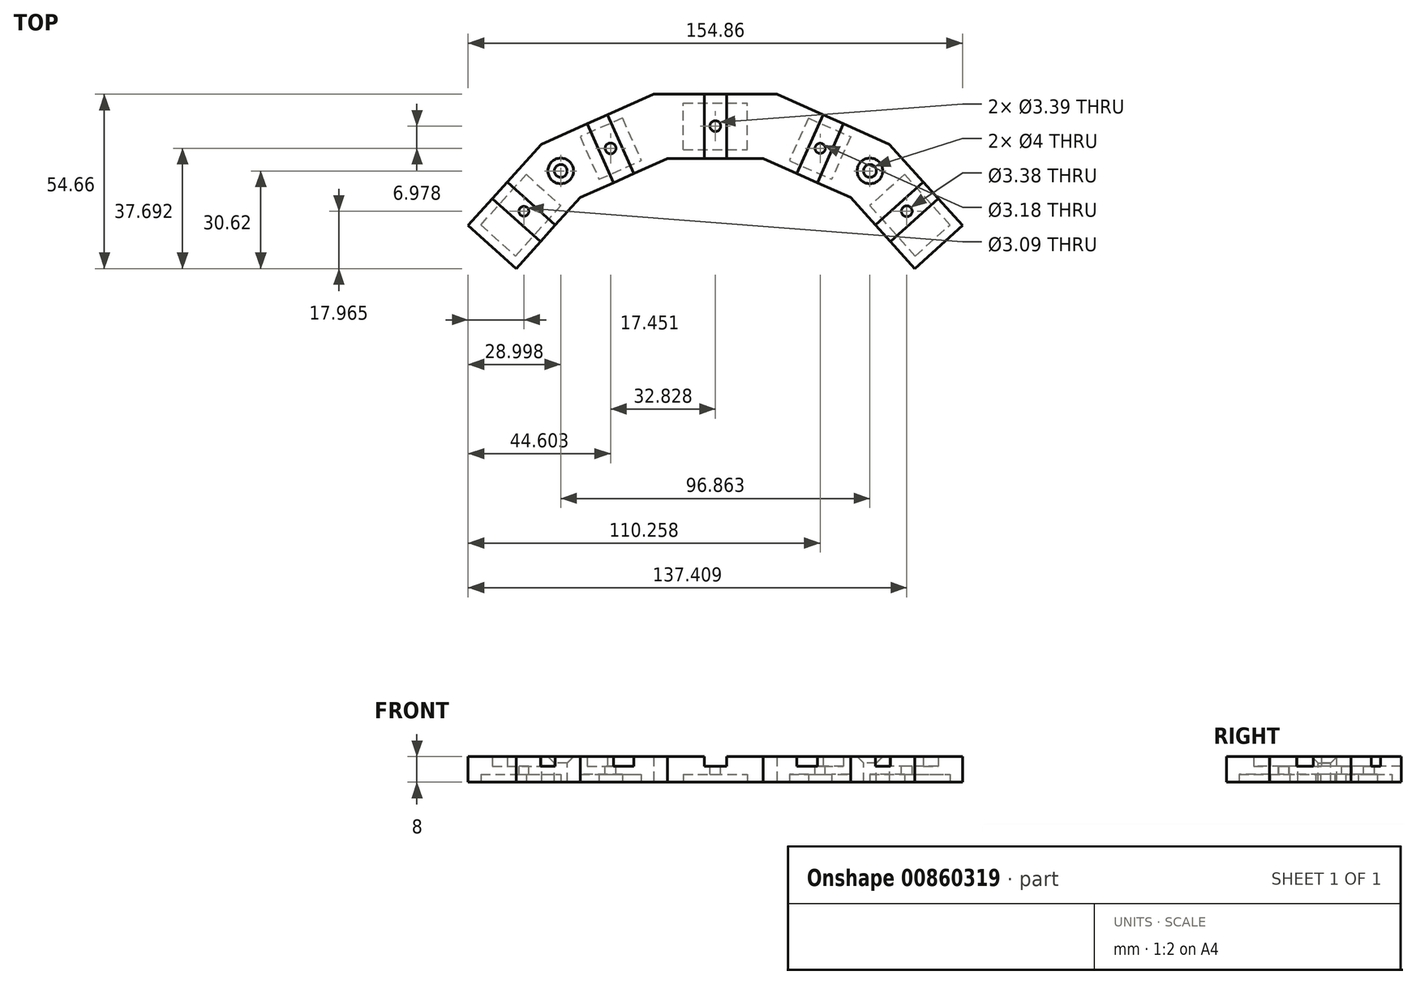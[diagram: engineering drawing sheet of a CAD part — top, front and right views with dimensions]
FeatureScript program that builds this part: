
annotation { "Feature Type Name" : "Feature", "Feature Type Description" : "" }
export const myFeature = defineFeature(function(context is Context, id is Id, definition is map)
    precondition{}
    {
        {
            var Q0;
            Q0=qCreatedBy(makeId("Top.planeOp"),FACE);
            var sketch = newSketch(context, id + "F0", { "sketchPlane" : qUnion([Q0])});
            skLineSegment(sketch, "E0.0", {"start": v(-14.98, 70.5) * mm, "end": v(14.98, 70.5) * mm});
            skLineSegment(sketch, "E0.1", {"start": v(14.98, 70.5) * mm, "end": v(42.36, 58.3) * mm});
            skLineSegment(sketch, "E0.2", {"start": v(42.36, 58.3) * mm, "end": v(62.42, 36.04) * mm});
            skLineSegment(sketch, "E0.13", {"start": v(-62.42, 36.04) * mm, "end": v(-42.36, 58.3) * mm});
            skLineSegment(sketch, "E0.14", {"start": v(-42.36, 58.3) * mm, "end": v(-14.98, 70.5) * mm});
            skPoint(sketch, "E0.0.midPoint", {"position": v(0, 70.5) * mm});
            skLineSegment(sketch, "E1.0", {"start": v(54.5, 75.01) * mm, "end": v(77.43, 49.55) * mm});
            skLineSegment(sketch, "E1.1", {"start": v(-77.43, 49.55) * mm, "end": v(-54.5, 75.01) * mm});
            skLineSegment(sketch, "E1.2", {"start": v(-54.5, 75.01) * mm, "end": v(-19.28, 90.7) * mm});
            skLineSegment(sketch, "E1.3", {"start": v(-19.28, 90.7) * mm, "end": v(19.28, 90.7) * mm});
            skLineSegment(sketch, "E1.4", {"start": v(19.28, 90.7) * mm, "end": v(54.5, 75.01) * mm});
            skLineSegment(sketch, "E2", {"start": v(-77.43, 49.55) * mm, "end": v(-62.42, 36.04) * mm});
            skLineSegment(sketch, "E3", {"start": v(62.42, 36.04) * mm, "end": v(77.43, 49.55) * mm});
            skPoint(sketch, "E0.cCircle.center.orphan", {"position": v(0, 0) * mm});
            skSolve(sketch);
        }
        {
            var Q0;
            Q0 = qSketchRegion(id + "F0", true);
            extrude(context, id + "F1", {"entities" : qUnion([Q0]), "depth" : 5 * mm, "offsetDistance" : 25 * mm});
        }
        {
            var Q0;
            Q0=makeQuery(id+"F1.opExtrude","CAP_FACE",FACE,{"disambiguationData":[OSD([sQuery(id+"F0.wireOp",EDGE,"E0.0"),sQuery(id+"F0.wireOp",EDGE,"E0.1"),sQuery(id+"F0.wireOp",EDGE,"E0.2"),sQuery(id+"F0.wireOp",EDGE,"E0.13"),sQuery(id+"F0.wireOp",EDGE,"E0.14"),sQuery(id+"F0.wireOp",EDGE,"E1.0"),sQuery(id+"F0.wireOp",EDGE,"E1.1"),sQuery(id+"F0.wireOp",EDGE,"E1.2"),sQuery(id+"F0.wireOp",EDGE,"E1.3"),sQuery(id+"F0.wireOp",EDGE,"E1.4"),sQuery(id+"F0.wireOp",EDGE,"E2"),sQuery(id+"F0.wireOp",EDGE,"E3")])],"isStart":false});
            var sketch = newSketch(context, id + "F2", { "sketchPlane" : qUnion([Q0])});
            skLineSegment(sketch, "E4", {"start": v(0, 90.7) * mm, "end": v(0, 70.5) * mm});
            skLineSegment(sketch, "E5.left", {"start": v(3.5, 90.7) * mm, "end": v(3.5, 70.5) * mm});
            skLineSegment(sketch, "E5.right", {"start": v(-3.5, 90.7) * mm, "end": v(-3.5, 70.5) * mm});
            skPoint(sketch, "E5.middle", {"position": v(0, 80.6) * mm});
            skPoint(sketch, "E6.center", {"position": v(0, 0) * mm});
            skLineSegment(sketch, "E7.1.1", {"start": v(33.76, 84.25) * mm, "end": v(25.53, 65.8) * mm});
            skLineSegment(sketch, "E7.1.2", {"start": v(40.16, 81.4) * mm, "end": v(31.93, 62.95) * mm});
            skLineSegment(sketch, "E7.2.1", {"start": v(65.16, 63.17) * mm, "end": v(50.13, 49.68) * mm});
            skLineSegment(sketch, "E7.2.2", {"start": v(69.85, 57.97) * mm, "end": v(54.81, 44.48) * mm});
            skLineSegment(sketch, "E8.MirrorCS", {"start": v(-33.76, 84.25) * mm, "end": v(-25.53, 65.8) * mm});
            skLineSegment(sketch, "E9.MirrorCS", {"start": v(-40.16, 81.4) * mm, "end": v(-31.93, 62.95) * mm});
            skLineSegment(sketch, "E10.MirrorCS", {"start": v(-69.85, 57.97) * mm, "end": v(-54.81, 44.48) * mm});
            skLineSegment(sketch, "E11.MirrorCS", {"start": v(-65.16, 63.17) * mm, "end": v(-50.13, 49.68) * mm});
            skLineSegment(sketch, "E12", {"start": v(-69.85, 57.97) * mm, "end": v(-77.43, 49.55) * mm});
            skLineSegment(sketch, "E13", {"start": v(-77.43, 49.55) * mm, "end": v(-62.42, 36.04) * mm});
            skLineSegment(sketch, "E14", {"start": v(-62.42, 36.04) * mm, "end": v(-54.81, 44.48) * mm});
            skPoint(sketch, "E15.MirrorCS.end.orphan", {"position": v(-65.16, 63.17) * mm});
            skPoint(sketch, "E16.MirrorCS.end.orphan", {"position": v(-50.13, 49.68) * mm});
            skPoint(sketch, "E16.MirrorCS.start.orphan", {"position": v(-54.81, 44.48) * mm});
            skLineSegment(sketch, "E17", {"start": v(-65.16, 63.17) * mm, "end": v(-54.5, 75.01) * mm});
            skLineSegment(sketch, "E18", {"start": v(-54.5, 75.01) * mm, "end": v(-40.16, 81.4) * mm});
            skLineSegment(sketch, "E19", {"start": v(-31.93, 62.95) * mm, "end": v(-42.36, 58.3) * mm});
            skLineSegment(sketch, "E20", {"start": v(-42.36, 58.3) * mm, "end": v(-50.13, 49.68) * mm});
            skLineSegment(sketch, "E21", {"start": v(-33.76, 84.25) * mm, "end": v(-19.28, 90.7) * mm});
            skLineSegment(sketch, "E22", {"start": v(-19.28, 90.7) * mm, "end": v(-3.5, 90.7) * mm});
            skLineSegment(sketch, "E23", {"start": v(-3.5, 70.5) * mm, "end": v(-14.98, 70.5) * mm});
            skLineSegment(sketch, "E24", {"start": v(-14.98, 70.5) * mm, "end": v(-25.53, 65.8) * mm});
            skLineSegment(sketch, "E25", {"start": v(3.5, 90.7) * mm, "end": v(19.28, 90.7) * mm});
            skLineSegment(sketch, "E26", {"start": v(19.28, 90.7) * mm, "end": v(33.76, 84.25) * mm});
            skLineSegment(sketch, "E27", {"start": v(3.5, 70.5) * mm, "end": v(14.98, 70.5) * mm});
            skLineSegment(sketch, "E28", {"start": v(14.98, 70.5) * mm, "end": v(25.53, 65.8) * mm});
            skLineSegment(sketch, "E29", {"start": v(40.16, 81.4) * mm, "end": v(54.5, 75.01) * mm});
            skLineSegment(sketch, "E30", {"start": v(54.5, 75.01) * mm, "end": v(65.16, 63.17) * mm});
            skLineSegment(sketch, "E31", {"start": v(31.93, 62.95) * mm, "end": v(42.36, 58.3) * mm});
            skLineSegment(sketch, "E32", {"start": v(42.36, 58.3) * mm, "end": v(50.13, 49.68) * mm});
            skLineSegment(sketch, "E33", {"start": v(69.85, 57.97) * mm, "end": v(77.43, 49.55) * mm});
            skLineSegment(sketch, "E34", {"start": v(77.43, 49.55) * mm, "end": v(62.42, 36.04) * mm});
            skLineSegment(sketch, "E35", {"start": v(62.42, 36.04) * mm, "end": v(54.81, 44.48) * mm});
            skPoint(sketch, "E36.MirrorCS.end.orphan", {"position": v(-33.76, 84.25) * mm});
            skPoint(sketch, "E36.MirrorCS.start.orphan", {"position": v(-40.16, 81.4) * mm});
            skPoint(sketch, "E37.MirrorCS.end.orphan", {"position": v(-25.53, 65.8) * mm});
            skPoint(sketch, "E37.MirrorCS.start.orphan", {"position": v(-31.93, 62.95) * mm});
            skSolve(sketch);
        }
        {
            var Q0;
            Q0 = qSketchRegion(id + "F2", true);
            var Q1;
            Q1=makeQuery(id+"F2.imprint","IMPRINT",FACE,{"disambiguationData":[TD([[makeQuery(id+"F2.imprint","IMPRINT",EDGE,{"derivedFrom":sQuery(id+"F2.wireOp",EDGE,"E5.right")}),-1.0]])]});
            extrude(context, id + "F3", {"entities" : qUnion([Q0, Q1]), "operationType" : NewBodyOperationType.ADD, "depth" : 3 * mm, "offsetDistance" : 25 * mm});
        }
        {
            var Q0;
            {var subQ0=sQuery(id+"F0.wireOp",EDGE,"E1.2");var subQ1=sQuery(id+"F0.wireOp",EDGE,"E0.14");Q0=makeQuery(id+"F3.boolean.opBoolean","SPLIT",FACE,{"disambiguationData":[TD([makeQuery(id+"F1.opExtrude","SWEPT_FACE",FACE,{"disambiguationData":[OSD([subQ1])]})])],"derivedFrom":makeQuery(id+"F1.opExtrude","CAP_FACE",FACE,{"disambiguationData":[OSD([sQuery(id+"F0.wireOp",EDGE,"E0.0"),sQuery(id+"F0.wireOp",EDGE,"E0.1"),sQuery(id+"F0.wireOp",EDGE,"E0.2"),sQuery(id+"F0.wireOp",EDGE,"E0.13"),subQ1,sQuery(id+"F0.wireOp",EDGE,"E1.0"),sQuery(id+"F0.wireOp",EDGE,"E1.1"),subQ0,sQuery(id+"F0.wireOp",EDGE,"E1.3"),sQuery(id+"F0.wireOp",EDGE,"E1.4"),sQuery(id+"F0.wireOp",EDGE,"E2"),sQuery(id+"F0.wireOp",EDGE,"E3")])],"isStart":false})});}
            var sketch = newSketch(context, id + "F4", { "sketchPlane" : qUnion([Q0])});
            skLineSegment(sketch, "E38", {"start": v(0, 90.78) * mm, "end": v(0, 70.64) * mm});
            skPoint(sketch, "E39", {"position": v(0, 80.7) * mm});
            skPoint(sketch, "E40.1.0", {"position": v(32.83, 73.73) * mm});
            skPoint(sketch, "E40.2.0", {"position": v(59.98, 54) * mm});
            skPoint(sketch, "E40.center", {"position": v(0, 0) * mm});
            skLineSegment(sketch, "E40.anchor1", {"start": v(0, 0) * mm, "end": v(0, 80.7) * mm, "construction": true});
            skLineSegment(sketch, "E40.anchor2", {"start": v(0, 0) * mm, "end": v(59.98, 54) * mm, "construction": true});
            skPoint(sketch, "E41.MirrorP", {"position": v(-32.83, 73.73) * mm});
            skPoint(sketch, "E42.MirrorP", {"position": v(-59.98, 54) * mm});
            skCircle(sketch, "E43", {"center": v(-59.98, 54) * mm, "radius": 1.55 * mm});
            skCircle(sketch, "E44", {"center": v(-32.83, 73.73) * mm, "radius": 1.7 * mm});
            skCircle(sketch, "E45", {"center": v(0, 80.7) * mm, "radius": 1.7 * mm});
            skCircle(sketch, "E46", {"center": v(32.83, 73.73) * mm, "radius": 1.6 * mm});
            skCircle(sketch, "E47", {"center": v(59.98, 54) * mm, "radius": 1.69 * mm});
            skSolve(sketch);
        }
        {
            var Q0;
            Q0=makeQuery(id+"F3.opExtrude","CAP_FACE",FACE,{"disambiguationData":[OSD([sQuery(id+"F2.wireOp",EDGE,"E9.MirrorCS"),sQuery(id+"F2.wireOp",EDGE,"E11.MirrorCS"),sQuery(id+"F2.wireOp",EDGE,"E17"),sQuery(id+"F2.wireOp",EDGE,"E18"),sQuery(id+"F2.wireOp",EDGE,"E19"),sQuery(id+"F2.wireOp",EDGE,"E20")])],"isStart":false});
            var sketch = newSketch(context, id + "F5", { "sketchPlane" : qUnion([Q0])});
            skLineSegment(sketch, "E48", {"start": v(-54.5, 75.01) * mm, "end": v(-42.36, 58.3) * mm});
            skPoint(sketch, "E49", {"position": v(-48.43, 66.66) * mm});
            skLineSegment(sketch, "E50", {"start": v(0, 91.15) * mm, "end": v(0, 71.4) * mm});
            skPoint(sketch, "E51.MirrorP", {"position": v(48.43, 66.66) * mm});
            skSolve(sketch);
        }
        {
            var Q0;
            Q0=sQuery(id+"F5.wireOp",VERTEX,"E49");
            var Q1;
            Q1=sQuery(id+"F5.wireOp",VERTEX,"E51.MirrorP");
            var Q2;
            Q2=makeQuery(id+"F1.opExtrude","SWEPT_BODY",BODY,{"disambiguationData":[OSD([sQuery(id+"F0.wireOp",EDGE,"E0.0"),sQuery(id+"F0.wireOp",EDGE,"E0.1"),sQuery(id+"F0.wireOp",EDGE,"E0.2"),sQuery(id+"F0.wireOp",EDGE,"E0.13"),sQuery(id+"F0.wireOp",EDGE,"E0.14"),sQuery(id+"F0.wireOp",EDGE,"E1.0"),sQuery(id+"F0.wireOp",EDGE,"E1.1"),sQuery(id+"F0.wireOp",EDGE,"E1.2"),sQuery(id+"F0.wireOp",EDGE,"E1.3"),sQuery(id+"F0.wireOp",EDGE,"E1.4"),sQuery(id+"F0.wireOp",EDGE,"E2"),sQuery(id+"F0.wireOp",EDGE,"E3")])]});
            hole(context, id + "F6", {"style" : HoleStyle.C_SINK, "endStyle" : HoleEndStyle.THROUGH, "standardTappedOrClearance" : lookupTablePath({ "standard" : "ISO", "size" : "4", "type" : "Drilled" }), "standardBlindInLast" : lookupTablePath({ "standard" : "ISO", "size" : "4", "type" : "Drilled" }), "holeDiameter" : 4 * mm, "cSinkDiameter" : 8 * mm, "cSinkAngle" : 90 * degree, "majorDiameter" : 5 * mm, "isTappedThrough" : true, "tappedDepth" : 12 * mm, "tapClearance" : 3, "locations" : qUnion([Q0, Q1]), "scope" : qUnion([Q2])});
        }
        {
            var Q0;
            Q0 = qSketchRegion(id + "F4", true);
            extrude(context, id + "F7", {"entities" : qUnion([Q0]), "operationType" : NewBodyOperationType.REMOVE, "oppositeDirection" : true, "depth" : 11.1 * mm, "offsetDistance" : 25 * mm});
        }
        {
            var Q0;
            Q0=makeQuery(id+"F1.opExtrude","CAP_FACE",FACE,{"disambiguationData":[OSD([sQuery(id+"F0.wireOp",EDGE,"E0.0"),sQuery(id+"F0.wireOp",EDGE,"E0.1"),sQuery(id+"F0.wireOp",EDGE,"E0.2"),sQuery(id+"F0.wireOp",EDGE,"E0.13"),sQuery(id+"F0.wireOp",EDGE,"E0.14"),sQuery(id+"F0.wireOp",EDGE,"E1.0"),sQuery(id+"F0.wireOp",EDGE,"E1.1"),sQuery(id+"F0.wireOp",EDGE,"E1.2"),sQuery(id+"F0.wireOp",EDGE,"E1.3"),sQuery(id+"F0.wireOp",EDGE,"E1.4"),sQuery(id+"F0.wireOp",EDGE,"E2"),sQuery(id+"F0.wireOp",EDGE,"E3")])],"isStart":true});
            var sketch = newSketch(context, id + "F8", { "sketchPlane" : qUnion([Q0])});
            skLineSegment(sketch, "E52.1", {"start": v(48.4, -55.78) * mm, "end": v(62.62, -39.99) * mm});
            skLineSegment(sketch, "E52.2", {"start": v(62.62, -39.99) * mm, "end": v(73.47, -49.76) * mm});
            skLineSegment(sketch, "E52.3", {"start": v(59.26, -65.55) * mm, "end": v(73.47, -49.76) * mm});
            skLineSegment(sketch, "E52.4", {"start": v(29.14, -83.24) * mm, "end": v(42.36, -77.35) * mm});
            skLineSegment(sketch, "E52.5", {"start": v(23.2, -69.9) * mm, "end": v(36.42, -64.02) * mm});
            skLineSegment(sketch, "E52.6", {"start": v(-10.05, -87.9) * mm, "end": v(10.05, -87.9) * mm});
            skLineSegment(sketch, "E52.7", {"start": v(0, -73.3) * mm, "end": v(10.05, -73.3) * mm});
            skLineSegment(sketch, "E52.8", {"start": v(-36.42, -64.02) * mm, "end": v(-23.2, -69.9) * mm});
            skLineSegment(sketch, "E52.9", {"start": v(-62.62, -39.99) * mm, "end": v(-48.4, -55.78) * mm});
            skLineSegment(sketch, "E52.10", {"start": v(-73.47, -49.76) * mm, "end": v(-62.62, -39.99) * mm});
            skLineSegment(sketch, "E52.11", {"start": v(-73.47, -49.76) * mm, "end": v(-59.26, -65.55) * mm});
            skLineSegment(sketch, "E53.bottom", {"start": v(10.05, -73.3) * mm, "end": v(-10.05, -73.3) * mm});
            skLineSegment(sketch, "E53.left", {"start": v(10.05, -73.3) * mm, "end": v(10.05, -87.9) * mm});
            skLineSegment(sketch, "E53.right", {"start": v(-10.05, -73.3) * mm, "end": v(-10.05, -87.9) * mm});
            skPoint(sketch, "E53.middle", {"position": v(0, -80.7) * mm});
            skPoint(sketch, "E54.orphan", {"position": v(10.05, -88.12) * mm});
            skPoint(sketch, "E55.orphan", {"position": v(-10.05, -88.12) * mm});
            skLineSegment(sketch, "E56", {"start": v(42.36, -77.35) * mm, "end": v(36.42, -64.02) * mm});
            skPoint(sketch, "E57.MirrorCS.end.orphan", {"position": v(43.98, -63.19) * mm});
            skPoint(sketch, "E57.MirrorCS.start.orphan", {"position": v(46.05, -67.84) * mm});
            skLineSegment(sketch, "E58.MirrorCS", {"start": v(29.14, -83.24) * mm, "end": v(23.2, -69.9) * mm});
            skLineSegment(sketch, "E59", {"start": v(59.26, -65.55) * mm, "end": v(48.4, -55.78) * mm});
            skPoint(sketch, "E60.MirrorCS.end.orphan", {"position": v(58.24, -44.85) * mm});
            skPoint(sketch, "E60.MirrorCS.start.orphan", {"position": v(69.1, -54.62) * mm});
            skPoint(sketch, "E61.start.orphan", {"position": v(59.98, -54) * mm});
            skPoint(sketch, "E62.endSnap0", {"position": v(0, -70.5) * mm});
            skPoint(sketch, "E63.end.orphan", {"position": v(30.75, -69.07) * mm});
            skPoint(sketch, "E63.start.orphan", {"position": v(32.83, -73.73) * mm});
            skPoint(sketch, "E64.MirrorP", {"position": v(-43.98, -63.19) * mm});
            skPoint(sketch, "E65.MirrorP", {"position": v(-46.05, -67.84) * mm});
            skLineSegment(sketch, "E66.MirrorCS", {"start": v(-59.26, -65.55) * mm, "end": v(-73.47, -49.76) * mm});
            skLineSegment(sketch, "E67.MirrorCS", {"start": v(-23.2, -69.9) * mm, "end": v(-36.42, -64.02) * mm});
            skLineSegment(sketch, "E68.MirrorCS", {"start": v(-59.26, -65.55) * mm, "end": v(-48.4, -55.78) * mm});
            skLineSegment(sketch, "E69.MirrorCS", {"start": v(-29.14, -83.24) * mm, "end": v(-42.36, -77.35) * mm});
            skPoint(sketch, "E70.MirrorP", {"position": v(-30.75, -69.07) * mm});
            skPoint(sketch, "E71.MirrorP", {"position": v(-32.83, -73.73) * mm});
            skPoint(sketch, "E72.MirrorP", {"position": v(-69.1, -54.62) * mm});
            skLineSegment(sketch, "E73.MirrorCS", {"start": v(-42.36, -77.35) * mm, "end": v(-36.42, -64.02) * mm});
            skLineSegment(sketch, "E74.MirrorCS", {"start": v(-62.62, -39.99) * mm, "end": v(-73.47, -49.76) * mm});
            skPoint(sketch, "E75.MirrorP", {"position": v(-59.98, -54) * mm});
            skPoint(sketch, "E76.MirrorP", {"position": v(-58.24, -44.85) * mm});
            skLineSegment(sketch, "E77.MirrorCS", {"start": v(-48.4, -55.78) * mm, "end": v(-62.62, -39.99) * mm});
            skLineSegment(sketch, "E78.MirrorCS", {"start": v(-29.14, -83.24) * mm, "end": v(-23.2, -69.9) * mm});
            skPoint(sketch, "E79.orphan", {"position": v(0, -63.34) * mm});
            skSolve(sketch);
        }
        {
            var Q0;
            Q0 = qSketchRegion(id + "F8", true);
            extrude(context, id + "F9", {"entities" : qUnion([Q0]), "operationType" : NewBodyOperationType.REMOVE, "oppositeDirection" : true, "depth" : 2.5 * mm, "offsetDistance" : 25 * mm});
        }
        {
            var Q0;
            {var subQ0=sQuery(id+"F0.wireOp",EDGE,"E1.1");var subQ1=sQuery(id+"F0.wireOp",EDGE,"E0.13");Q0=makeQuery(id+"F3.boolean.opBoolean","SPLIT",FACE,{"disambiguationData":[TD([makeQuery(id+"F1.opExtrude","SWEPT_FACE",FACE,{"disambiguationData":[OSD([subQ1])]})])],"derivedFrom":makeQuery(id+"F1.opExtrude","CAP_FACE",FACE,{"disambiguationData":[OSD([sQuery(id+"F0.wireOp",EDGE,"E0.0"),sQuery(id+"F0.wireOp",EDGE,"E0.1"),sQuery(id+"F0.wireOp",EDGE,"E0.2"),subQ1,sQuery(id+"F0.wireOp",EDGE,"E0.14"),sQuery(id+"F0.wireOp",EDGE,"E1.0"),subQ0,sQuery(id+"F0.wireOp",EDGE,"E1.2"),sQuery(id+"F0.wireOp",EDGE,"E1.3"),sQuery(id+"F0.wireOp",EDGE,"E1.4"),sQuery(id+"F0.wireOp",EDGE,"E2"),sQuery(id+"F0.wireOp",EDGE,"E3")])],"isStart":false})});}
            var sketch = newSketch(context, id + "F10", { "sketchPlane" : qUnion([Q0])});
            skLineSegment(sketch, "E80", {"start": v(-65.16, 63.17) * mm, "end": v(-69.85, 57.97) * mm});
            skLineSegment(sketch, "E81", {"start": v(-69.85, 57.97) * mm, "end": v(-54.81, 44.48) * mm});
            skLineSegment(sketch, "E82", {"start": v(-54.81, 44.48) * mm, "end": v(-50.13, 49.68) * mm});
            skLineSegment(sketch, "E83", {"start": v(-50.13, 49.68) * mm, "end": v(-65.16, 63.17) * mm});
            skCircle(sketch, "E84", {"center": v(-59.98, 54) * mm, "radius": 1.5 * mm});
            skSolve(sketch);
        }
        {
            var Q0;
            Q0 = qSketchRegion(id + "F10", true);
            extrude(context, id + "F11", {"entities" : qUnion([Q0]), "depth" : 1 * mm, "offsetDistance" : 25 * mm});
        }
        {
            var Q0;
            {var subQ0=sQuery(id+"F0.wireOp",EDGE,"E1.2");var subQ1=sQuery(id+"F0.wireOp",EDGE,"E0.14");Q0=makeQuery(id+"F3.boolean.opBoolean","SPLIT",FACE,{"disambiguationData":[TD([makeQuery(id+"F1.opExtrude","SWEPT_FACE",FACE,{"disambiguationData":[OSD([subQ1])]})])],"derivedFrom":makeQuery(id+"F1.opExtrude","CAP_FACE",FACE,{"disambiguationData":[OSD([sQuery(id+"F0.wireOp",EDGE,"E0.0"),sQuery(id+"F0.wireOp",EDGE,"E0.1"),sQuery(id+"F0.wireOp",EDGE,"E0.2"),sQuery(id+"F0.wireOp",EDGE,"E0.13"),subQ1,sQuery(id+"F0.wireOp",EDGE,"E1.0"),sQuery(id+"F0.wireOp",EDGE,"E1.1"),subQ0,sQuery(id+"F0.wireOp",EDGE,"E1.3"),sQuery(id+"F0.wireOp",EDGE,"E1.4"),sQuery(id+"F0.wireOp",EDGE,"E2"),sQuery(id+"F0.wireOp",EDGE,"E3")])],"isStart":false})});}
            var sketch = newSketch(context, id + "F12", { "sketchPlane" : qUnion([Q0])});
            skLineSegment(sketch, "E85", {"start": v(-33.76, 84.25) * mm, "end": v(-40.16, 81.4) * mm});
            skLineSegment(sketch, "E86", {"start": v(-40.16, 81.4) * mm, "end": v(-31.93, 62.95) * mm});
            skLineSegment(sketch, "E87", {"start": v(-31.93, 62.95) * mm, "end": v(-25.53, 65.8) * mm});
            skLineSegment(sketch, "E88", {"start": v(-25.53, 65.8) * mm, "end": v(-33.76, 84.25) * mm});
            skCircle(sketch, "E89", {"center": v(-32.83, 73.73) * mm, "radius": 1.67 * mm});
            skSolve(sketch);
        }
        {
            var Q0;
            Q0 = qSketchRegion(id + "F12", true);
            extrude(context, id + "F13", {"entities" : qUnion([Q0]), "depth" : 1 * mm, "offsetDistance" : 25 * mm});
        }
        {
            var Q0;
            {var subQ0=sQuery(id+"F0.wireOp",EDGE,"E1.3");var subQ1=sQuery(id+"F0.wireOp",EDGE,"E0.0");Q0=makeQuery(id+"F3.boolean.opBoolean","SPLIT",FACE,{"disambiguationData":[TD([makeQuery(id+"F1.opExtrude","SWEPT_FACE",FACE,{"disambiguationData":[OSD([subQ1])]})])],"derivedFrom":makeQuery(id+"F1.opExtrude","CAP_FACE",FACE,{"disambiguationData":[OSD([subQ1,sQuery(id+"F0.wireOp",EDGE,"E0.1"),sQuery(id+"F0.wireOp",EDGE,"E0.2"),sQuery(id+"F0.wireOp",EDGE,"E0.13"),sQuery(id+"F0.wireOp",EDGE,"E0.14"),sQuery(id+"F0.wireOp",EDGE,"E1.0"),sQuery(id+"F0.wireOp",EDGE,"E1.1"),sQuery(id+"F0.wireOp",EDGE,"E1.2"),subQ0,sQuery(id+"F0.wireOp",EDGE,"E1.4"),sQuery(id+"F0.wireOp",EDGE,"E2"),sQuery(id+"F0.wireOp",EDGE,"E3")])],"isStart":false})});}
            var sketch = newSketch(context, id + "F14", { "sketchPlane" : qUnion([Q0])});
            skLineSegment(sketch, "E90", {"start": v(-3.5, 90.7) * mm, "end": v(3.5, 90.7) * mm});
            skLineSegment(sketch, "E91", {"start": v(3.5, 90.7) * mm, "end": v(3.5, 70.5) * mm});
            skLineSegment(sketch, "E92", {"start": v(3.5, 70.5) * mm, "end": v(-3.5, 70.5) * mm});
            skLineSegment(sketch, "E93", {"start": v(-3.5, 70.5) * mm, "end": v(-3.5, 90.7) * mm});
            skCircle(sketch, "E94", {"center": v(0, 80.7) * mm, "radius": 1.62 * mm});
            skSolve(sketch);
        }
        {
            var Q0;
            Q0 = qSketchRegion(id + "F14", true);
            extrude(context, id + "F15", {"entities" : qUnion([Q0]), "depth" : 1 * mm, "offsetDistance" : 25 * mm});
        }
        {
            var Q0;
            {var subQ0=sQuery(id+"F0.wireOp",EDGE,"E1.4");var subQ1=sQuery(id+"F0.wireOp",EDGE,"E0.1");Q0=makeQuery(id+"F3.boolean.opBoolean","SPLIT",FACE,{"disambiguationData":[TD([makeQuery(id+"F1.opExtrude","SWEPT_FACE",FACE,{"disambiguationData":[OSD([subQ1])]})])],"derivedFrom":makeQuery(id+"F1.opExtrude","CAP_FACE",FACE,{"disambiguationData":[OSD([sQuery(id+"F0.wireOp",EDGE,"E0.0"),subQ1,sQuery(id+"F0.wireOp",EDGE,"E0.2"),sQuery(id+"F0.wireOp",EDGE,"E0.13"),sQuery(id+"F0.wireOp",EDGE,"E0.14"),sQuery(id+"F0.wireOp",EDGE,"E1.0"),sQuery(id+"F0.wireOp",EDGE,"E1.1"),sQuery(id+"F0.wireOp",EDGE,"E1.2"),sQuery(id+"F0.wireOp",EDGE,"E1.3"),subQ0,sQuery(id+"F0.wireOp",EDGE,"E2"),sQuery(id+"F0.wireOp",EDGE,"E3")])],"isStart":false})});}
            var sketch = newSketch(context, id + "F16", { "sketchPlane" : qUnion([Q0])});
            skLineSegment(sketch, "E95", {"start": v(33.76, 84.25) * mm, "end": v(40.16, 81.4) * mm});
            skLineSegment(sketch, "E96", {"start": v(40.16, 81.4) * mm, "end": v(31.93, 62.95) * mm});
            skLineSegment(sketch, "E97", {"start": v(31.93, 62.95) * mm, "end": v(25.53, 65.8) * mm});
            skLineSegment(sketch, "E98", {"start": v(25.53, 65.8) * mm, "end": v(33.76, 84.25) * mm});
            skCircle(sketch, "E99", {"center": v(32.83, 73.73) * mm, "radius": 1.64 * mm});
            skSolve(sketch);
        }
        {
            var Q0;
            Q0 = qSketchRegion(id + "F16", true);
            extrude(context, id + "F17", {"entities" : qUnion([Q0]), "depth" : 1 * mm, "offsetDistance" : 25 * mm});
        }
        {
            var Q0;
            {var subQ0=sQuery(id+"F0.wireOp",EDGE,"E1.0");var subQ1=sQuery(id+"F0.wireOp",EDGE,"E0.2");Q0=makeQuery(id+"F3.boolean.opBoolean","SPLIT",FACE,{"disambiguationData":[TD([makeQuery(id+"F1.opExtrude","SWEPT_FACE",FACE,{"disambiguationData":[OSD([subQ1])]})])],"derivedFrom":makeQuery(id+"F1.opExtrude","CAP_FACE",FACE,{"disambiguationData":[OSD([sQuery(id+"F0.wireOp",EDGE,"E0.0"),sQuery(id+"F0.wireOp",EDGE,"E0.1"),subQ1,sQuery(id+"F0.wireOp",EDGE,"E0.13"),sQuery(id+"F0.wireOp",EDGE,"E0.14"),subQ0,sQuery(id+"F0.wireOp",EDGE,"E1.1"),sQuery(id+"F0.wireOp",EDGE,"E1.2"),sQuery(id+"F0.wireOp",EDGE,"E1.3"),sQuery(id+"F0.wireOp",EDGE,"E1.4"),sQuery(id+"F0.wireOp",EDGE,"E2"),sQuery(id+"F0.wireOp",EDGE,"E3")])],"isStart":false})});}
            var sketch = newSketch(context, id + "F18", { "sketchPlane" : qUnion([Q0])});
            skLineSegment(sketch, "E100", {"start": v(65.16, 63.17) * mm, "end": v(69.85, 57.97) * mm});
            skLineSegment(sketch, "E101", {"start": v(69.85, 57.97) * mm, "end": v(54.81, 44.48) * mm});
            skLineSegment(sketch, "E102", {"start": v(54.81, 44.48) * mm, "end": v(50.13, 49.68) * mm});
            skLineSegment(sketch, "E103", {"start": v(50.13, 49.68) * mm, "end": v(65.16, 63.17) * mm});
            skCircle(sketch, "E104", {"center": v(59.98, 54) * mm, "radius": 1.67 * mm});
            skSolve(sketch);
        }
        {
            var Q0;
            Q0 = qSketchRegion(id + "F18", true);
            extrude(context, id + "F19", {"entities" : qUnion([Q0]), "depth" : 1 * mm, "offsetDistance" : 25 * mm});
        }
        {
            var Q0;
            Q0=makeQuery(id+"F11.opExtrude","SWEPT_BODY",BODY,{"disambiguationData":[OSD([sQuery(id+"F10.wireOp",EDGE,"E80"),sQuery(id+"F10.wireOp",EDGE,"E81"),sQuery(id+"F10.wireOp",EDGE,"E82"),sQuery(id+"F10.wireOp",EDGE,"E83"),sQuery(id+"F10.wireOp",EDGE,"E84")])]});
            var Q1;
            Q1=makeQuery(id+"F13.opExtrude","SWEPT_BODY",BODY,{"disambiguationData":[OSD([sQuery(id+"F12.wireOp",EDGE,"E85"),sQuery(id+"F12.wireOp",EDGE,"E86"),sQuery(id+"F12.wireOp",EDGE,"E87"),sQuery(id+"F12.wireOp",EDGE,"E88"),sQuery(id+"F12.wireOp",EDGE,"E89")])]});
            var Q2;
            Q2=makeQuery(id+"F15.opExtrude","SWEPT_BODY",BODY,{"disambiguationData":[OSD([sQuery(id+"F14.wireOp",EDGE,"E90"),sQuery(id+"F14.wireOp",EDGE,"E91"),sQuery(id+"F14.wireOp",EDGE,"E92"),sQuery(id+"F14.wireOp",EDGE,"E93"),sQuery(id+"F14.wireOp",EDGE,"E94")])]});
            var Q3;
            Q3=makeQuery(id+"F17.opExtrude","SWEPT_BODY",BODY,{"disambiguationData":[OSD([sQuery(id+"F16.wireOp",EDGE,"E95"),sQuery(id+"F16.wireOp",EDGE,"E96"),sQuery(id+"F16.wireOp",EDGE,"E97"),sQuery(id+"F16.wireOp",EDGE,"E98"),sQuery(id+"F16.wireOp",EDGE,"E99")])]});
            var Q4;
            Q4=makeQuery(id+"F19.opExtrude","SWEPT_BODY",BODY,{"disambiguationData":[OSD([sQuery(id+"F18.wireOp",EDGE,"E100"),sQuery(id+"F18.wireOp",EDGE,"E101"),sQuery(id+"F18.wireOp",EDGE,"E102"),sQuery(id+"F18.wireOp",EDGE,"E103"),sQuery(id+"F18.wireOp",EDGE,"E104")])]});
            deleteBodies(context, id + "F20", {"entities" : qUnion([Q0, Q1, Q2, Q3, Q4])});
        }
    });
